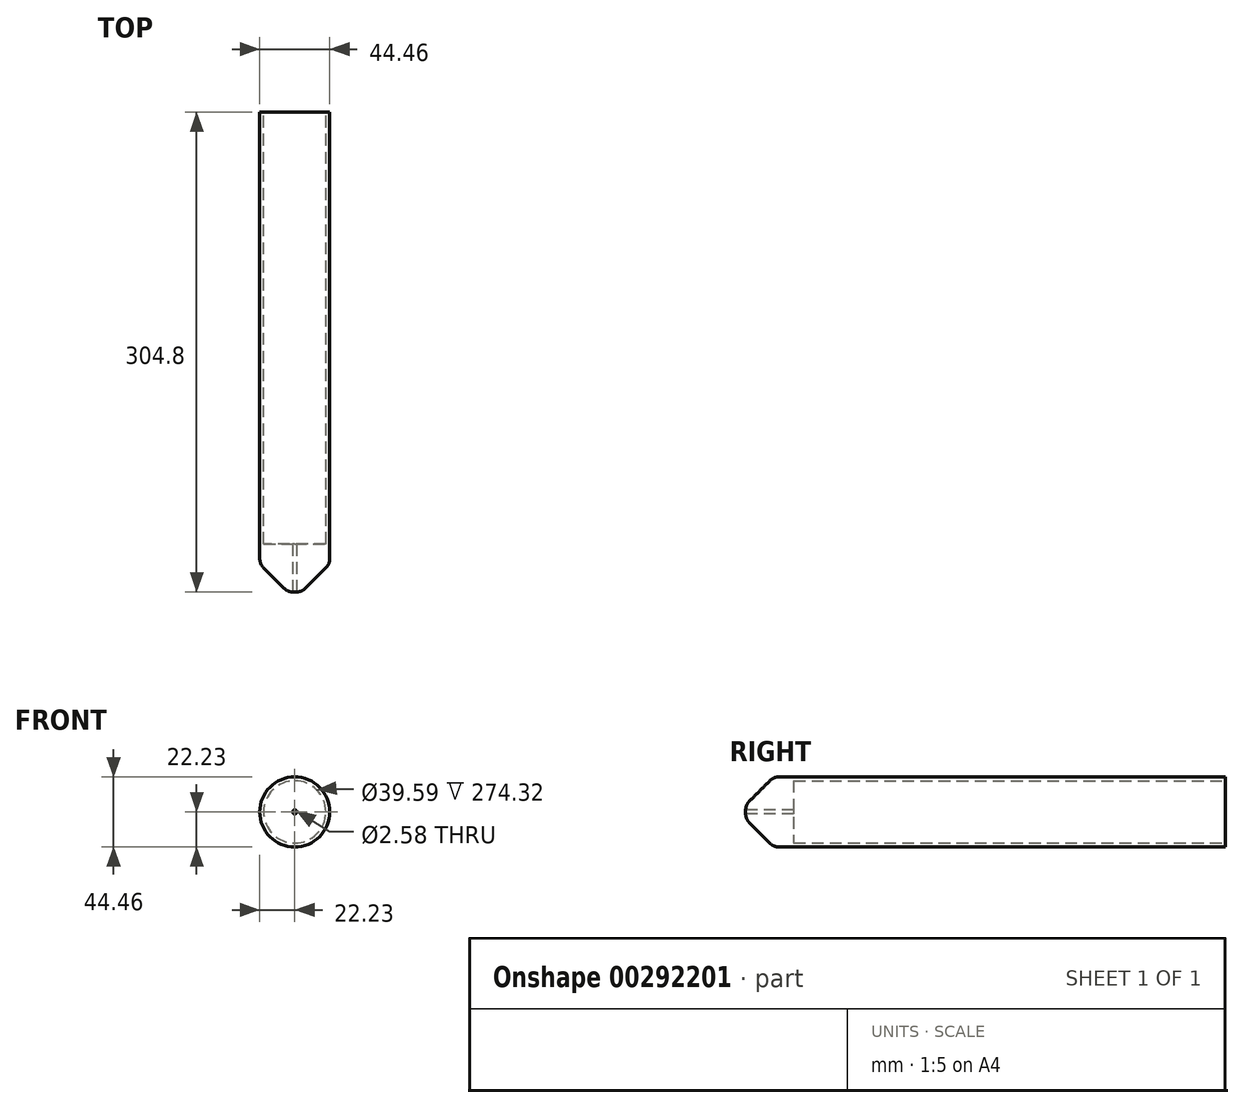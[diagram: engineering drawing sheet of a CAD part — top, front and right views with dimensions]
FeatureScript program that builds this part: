
annotation { "Feature Type Name" : "Feature", "Feature Type Description" : "" }
export const myFeature = defineFeature(function(context is Context, id is Id, definition is map)
    precondition{}
    {
        {
            var Q0;
            Q0=qCreatedBy(makeId("Front.planeOp"),FACE);
            var sketch = newSketch(context, id + "F0", { "sketchPlane" : qUnion([Q0])});
            skCircle(sketch, "E0", {"center": v(0, 0) * mm, "radius": 22.23 * mm});
            skSolve(sketch);
        }
        {
            var Q0;
            Q0=makeQuery(id+"F0.imprint","IMPRINT",FACE,{"disambiguationData":[TD([[makeQuery(id+"F0.imprint","IMPRINT",EDGE,{"derivedFrom":sQuery(id+"F0.wireOp",EDGE,"E0")}),1.0]])]});
            extrude(context, id + "F1", {"entities" : qUnion([Q0]), "depth" : 304.8 * mm});
        }
        {
            var Q0;
            Q0=makeQuery(id+"F1.opExtrude","CAP_EDGE",EDGE,{"disambiguationData":[OSD([sQuery(id+"F0.wireOp",EDGE,"E0")])],"isStart":false});
            chamfer(context, id + "F2", {"entities" : qUnion([Q0]), "width" : 17.78 * mm, "tangentPropagation" : true});
        }
        {
            var Q0;
            {var subQ0=sQuery(id+"F0.wireOp",EDGE,"E0");Q0=makeQuery(id+"F2.opChamfer","BLEND_EDGE",EDGE,{"blendedFrom":[makeQuery(id+"F1.opExtrude","CAP_EDGE",EDGE,{"disambiguationData":[OSD([subQ0])],"isStart":false}),makeQuery(id+"F1.opExtrude","CAP_FACE",FACE,{"disambiguationData":[OSD([subQ0])],"isStart":false})],"blendedInto":[makeQuery(id+"F1.opExtrude","CAP_FACE",FACE,{"disambiguationData":[OSD([subQ0])],"isStart":false})]});}
            fillet(context, id + "F3", {"entities" : qUnion([Q0]), "radius" : 7.62 * mm, "tangentPropagation" : true, "allowEdgeOverflow" : false});
        }
        {
            var Q0;
            {var subQ0=sQuery(id+"F0.wireOp",EDGE,"E0");Q0=makeQuery(id+"F2.opChamfer","BLEND_EDGE",EDGE,{"blendedFrom":[makeQuery(id+"F1.opExtrude","CAP_EDGE",EDGE,{"disambiguationData":[OSD([subQ0])],"isStart":false}),makeQuery(id+"F1.opExtrude","SWEPT_FACE",FACE,{"disambiguationData":[OSD([subQ0])]})],"blendedInto":[makeQuery(id+"F1.opExtrude","SWEPT_FACE",FACE,{"disambiguationData":[OSD([subQ0])]})]});}
            fillet(context, id + "F4", {"entities" : qUnion([Q0]), "radius" : 7.62 * mm, "tangentPropagation" : true, "allowEdgeOverflow" : false});
        }
        {
            var Q0;
            Q0=makeQuery(id+"F1.opExtrude","CAP_FACE",FACE,{"disambiguationData":[OSD([sQuery(id+"F0.wireOp",EDGE,"E0")])],"isStart":true});
            var sketch = newSketch(context, id + "F5", { "sketchPlane" : qUnion([Q0])});
            skCircle(sketch, "E1", {"center": v(0, 0) * mm, "radius": 19.8 * mm});
            skSolve(sketch);
        }
        {
            var Q0;
            Q0=makeQuery(id+"F5.imprint","IMPRINT",FACE,{"disambiguationData":[TD([[makeQuery(id+"F5.imprint","IMPRINT",EDGE,{"derivedFrom":sQuery(id+"F5.wireOp",EDGE,"E1")}),1.0]])]});
            var sketch = newSketch(context, id + "F6", { "sketchPlane" : qUnion([Q0])});
            skSolve(sketch);
        }
        {
            var Q0;
            Q0 = qSketchRegion(id + "F6", true);
            var Q1;
            Q1=makeQuery(id+"F6.imprint","IMPRINT",FACE,{"disambiguationData":[TD([[makeQuery(id+"F6.imprint","IMPRINT",EDGE,{"derivedFrom":makeQuery(id+"F5.imprint","IMPRINT",EDGE,{"derivedFrom":sQuery(id+"F5.wireOp",EDGE,"E1")})}),1.0]])]});
            extrude(context, id + "F7", {"entities" : qUnion([Q0, Q1]), "operationType" : NewBodyOperationType.REMOVE, "oppositeDirection" : true, "depth" : 274.32 * mm});
        }
        {
            var Q0;
            Q0=makeQuery(id+"F1.opExtrude","CAP_FACE",FACE,{"disambiguationData":[OSD([sQuery(id+"F0.wireOp",EDGE,"E0")])],"isStart":false});
            var sketch = newSketch(context, id + "F8", { "sketchPlane" : qUnion([Q0])});
            skSolve(sketch);
        }
        {
            var Q0;
            Q0 = qSketchRegion(id + "F8", true);
            var Q1;
            {var subQ0=sQuery(id+"F0.wireOp",EDGE,"E0");var subQ1=makeQuery(id+"F1.opExtrude","CAP_FACE",FACE,{"disambiguationData":[OSD([subQ0])],"isStart":false});Q1=makeQuery(id+"F8.imprint","IMPRINT",FACE,{"disambiguationData":[TD([[makeQuery(id+"F8.imprint","IMPRINT",EDGE,{"derivedFrom":makeQuery(id+"F3.opFillet","BLEND_EDGE",EDGE,{"blendedFrom":[makeQuery(id+"F2.opChamfer","BLEND_EDGE",EDGE,{"blendedFrom":[makeQuery(id+"F1.opExtrude","CAP_EDGE",EDGE,{"disambiguationData":[OSD([subQ0])],"isStart":false}),subQ1],"blendedInto":[subQ1]}),subQ1],"blendedInto":[subQ1]})}),1.0]])]});}
            extrude(context, id + "F9", {"entities" : qUnion([Q0, Q1]), "operationType" : NewBodyOperationType.REMOVE, "oppositeDirection" : true, "depth" : 304.8 * mm});
        }
    });
